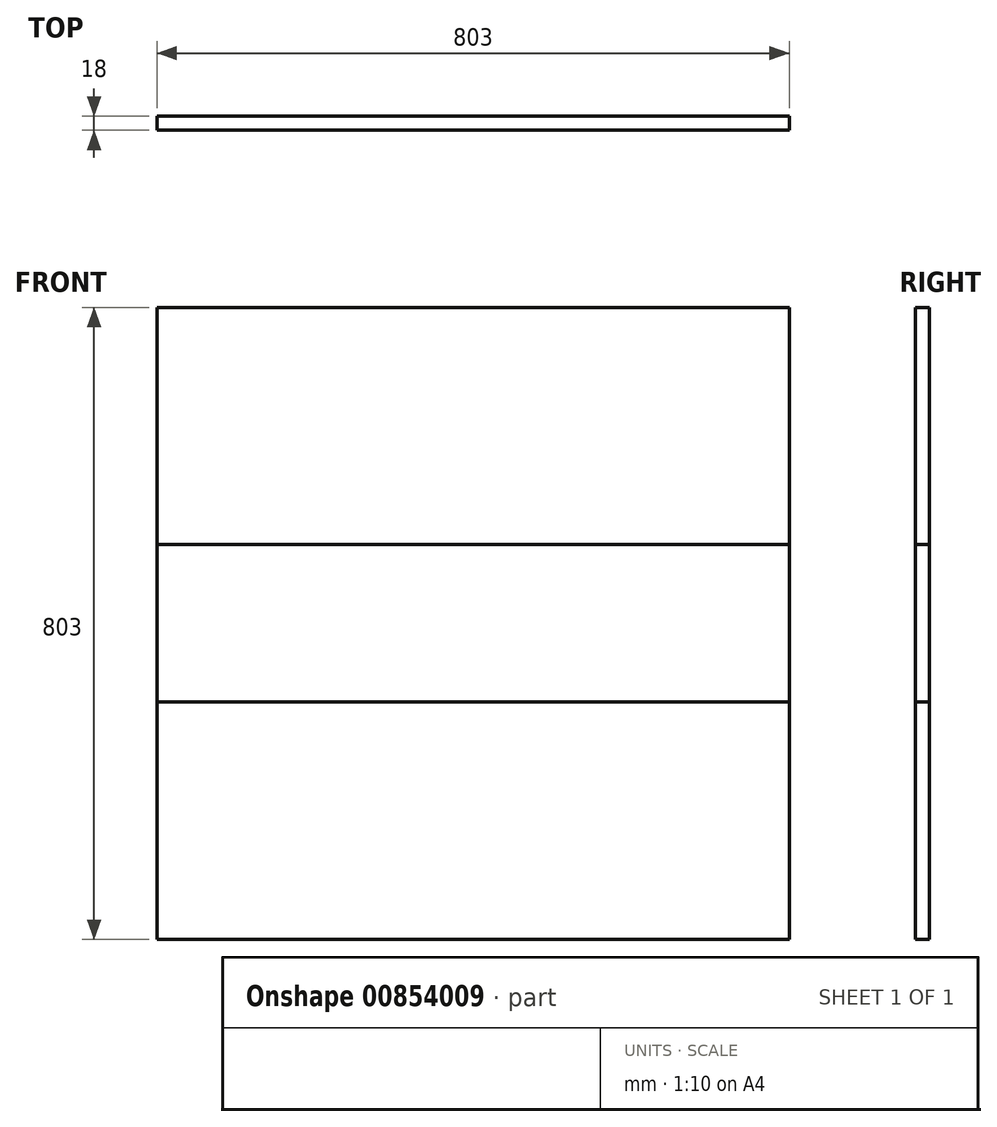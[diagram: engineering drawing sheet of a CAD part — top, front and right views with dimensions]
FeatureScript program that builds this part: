
annotation { "Feature Type Name" : "Feature", "Feature Type Description" : "" }
export const myFeature = defineFeature(function(context is Context, id is Id, definition is map)
    precondition{}
    {
        {
            var Q0;
            Q0=qCreatedBy(makeId("Front.planeOp"),FACE);
            var sketch = newSketch(context, id + "F0", { "sketchPlane" : qUnion([Q0])});
            skLineSegment(sketch, "E0.bottom", {"start": v(-401.5, 401.5) * mm, "end": v(401.5, 401.5) * mm});
            skLineSegment(sketch, "E0.top", {"start": v(-401.5, -401.5) * mm, "end": v(401.5, -401.5) * mm});
            skLineSegment(sketch, "E0.left", {"start": v(-401.5, 401.5) * mm, "end": v(-401.5, -401.5) * mm});
            skLineSegment(sketch, "E0.right", {"start": v(401.5, 401.5) * mm, "end": v(401.5, -401.5) * mm});
            skLineSegment(sketch, "E1", {"start": v(0, 0) * mm, "end": v(0, -401.5) * mm, "construction": true});
            skLineSegment(sketch, "E2", {"start": v(0, 0) * mm, "end": v(401.5, 0) * mm, "construction": true});
            skSolve(sketch);
        }
        {
            var Q0;
            Q0=makeQuery(id+"F0.imprint","IMPRINT",FACE,{"disambiguationData":[TD([[makeQuery(id+"F0.imprint","IMPRINT",EDGE,{"derivedFrom":sQuery(id+"F0.wireOp",EDGE,"E0.bottom")}),-1.0]])]});
            extrude(context, id + "F1", {"entities" : qUnion([Q0]), "depth" : 18 * mm, "offsetDistance" : 25 * mm});
        }
        {
            var Q0;
            Q0=makeQuery(id+"F0.imprint","IMPRINT",FACE,{"disambiguationData":[TD([[makeQuery(id+"F0.imprint","IMPRINT",EDGE,{"derivedFrom":sQuery(id+"F0.wireOp",EDGE,"E0.bottom")}),-1.0]])]});
            var sketch = newSketch(context, id + "F2", { "sketchPlane" : qUnion([Q0])});
            skLineSegment(sketch, "E3.bottom", {"start": v(-401.5, 100) * mm, "end": v(401.5, 100) * mm});
            skLineSegment(sketch, "E3.top", {"start": v(-401.5, -100) * mm, "end": v(401.5, -100) * mm});
            skLineSegment(sketch, "E3.left", {"start": v(-401.5, 100) * mm, "end": v(-401.5, -100) * mm});
            skLineSegment(sketch, "E3.right", {"start": v(401.5, 100) * mm, "end": v(401.5, -100) * mm});
            skLineSegment(sketch, "E4", {"start": v(0, 0) * mm, "end": v(0, -100) * mm, "construction": true});
            skLineSegment(sketch, "E5", {"start": v(0, 0) * mm, "end": v(401.5, 0) * mm, "construction": true});
            skSolve(sketch);
        }
        {
            var Q0;
            Q0=qSketchRegion(id+"F2",true);
            extrude(context, id + "F3", {"entities" : qUnion([Q0]), "depth" : 18 * mm, "offsetDistance" : 25 * mm});
        }
        {
            var Q0;
            {var subQ0=sQuery(id+"F2.wireOp",EDGE,"E3.top");Q0=makeQuery(id+"F2.imprint","IMPRINT",FACE,{"disambiguationData":[TD([[makeQuery(id+"F2.imprint","IMPRINT",EDGE,{"derivedFrom":subQ0}),-1.0]])]});}
            var sketch = newSketch(context, id + "F4", { "sketchPlane" : qUnion([Q0])});
            skLineSegment(sketch, "E6.bottom", {"start": v(-401.5, 100) * mm, "end": v(401.5, 100) * mm});
            skLineSegment(sketch, "E6.top", {"start": v(-401.5, -100) * mm, "end": v(401.5, -100) * mm});
            skLineSegment(sketch, "E6.left", {"start": v(-401.5, 100) * mm, "end": v(-401.5, -100) * mm});
            skLineSegment(sketch, "E6.right", {"start": v(401.5, 100) * mm, "end": v(401.5, -100) * mm});
            skLineSegment(sketch, "E7", {"start": v(0, 0) * mm, "end": v(0, -100) * mm, "construction": true});
            skLineSegment(sketch, "E8", {"start": v(0, 0) * mm, "end": v(401.5, 0) * mm, "construction": true});
            skPoint(sketch, "E9", {"position": v(0, 0) * mm});
            skSolve(sketch);
        }
        {
            var Q0;
            Q0=makeQuery(id+"F4.imprint","IMPRINT",FACE,{"disambiguationData":[TD([[makeQuery(id+"F4.imprint","IMPRINT",EDGE,{"derivedFrom":sQuery(id+"F4.wireOp",EDGE,"E6.bottom")}),-1.0]])]});
            extrude(context, id + "F5", {"entities" : qUnion([Q0]), "depth" : 18 * mm, "offsetDistance" : 25 * mm});
        }
    });
